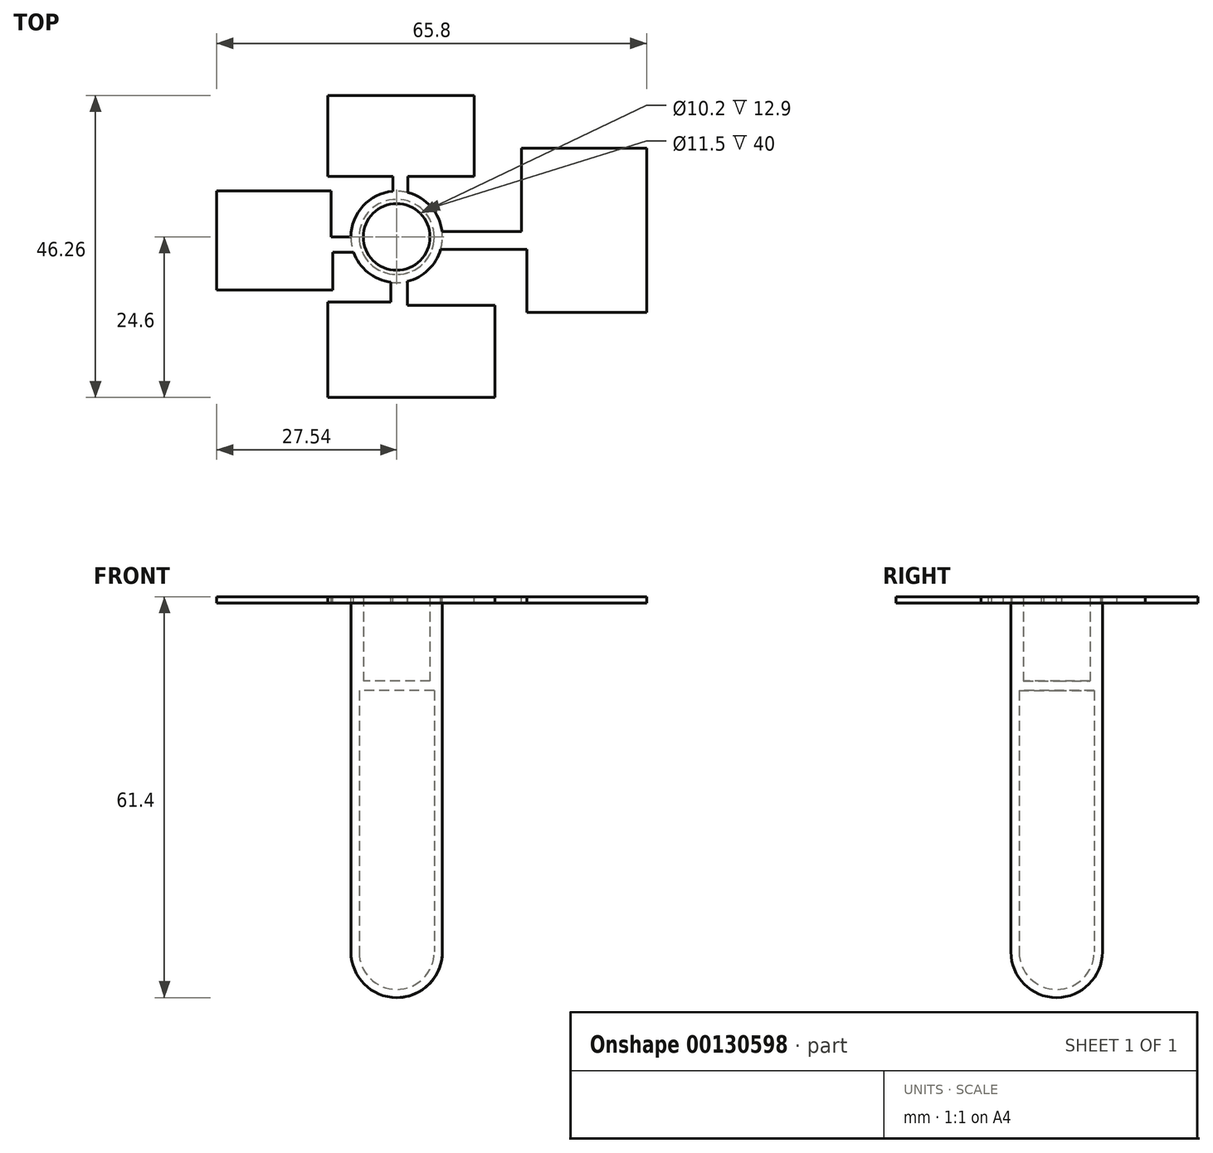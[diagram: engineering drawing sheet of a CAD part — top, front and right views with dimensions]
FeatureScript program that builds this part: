
annotation { "Feature Type Name" : "Feature", "Feature Type Description" : "" }
export const myFeature = defineFeature(function(context is Context, id is Id, definition is map)
    precondition{}
    {
        {
            var Q0;
            Q0=qCreatedBy(makeId("Top.planeOp"),FACE);
            var sketch = newSketch(context, id + "F0", { "sketchPlane" : qUnion([Q0])});
            skCircle(sketch, "E0", {"center": v(0, 0) * mm, "radius": 7 * mm});
            skCircle(sketch, "E1", {"center": v(0, 0) * mm, "radius": 5.75 * mm});
            skLineSegment(sketch, "E2", {"start": v(-5.75, 0) * mm, "end": v(5.75, 0) * mm});
            skSolve(sketch);
        }
        {
            var Q0;
            Q0=makeQuery(id+"F0.imprint","IMPRINT",FACE,{"disambiguationData":[TD([[makeQuery(id+"F0.imprint","IMPRINT",EDGE,{"derivedFrom":sQuery(id+"F0.wireOp",EDGE,"E0")}),1.0]])]});
            var Q1;
            {var subQ0=sQuery(id+"F0.wireOp",EDGE,"E2");Q1=makeQuery(id+"F0.imprint","IMPRINT",FACE,{"disambiguationData":[TD([[makeQuery(id+"F0.imprint","IMPRINT",EDGE,{"derivedFrom":subQ0}),1.0]])]});}
            var Q2;
            {var subQ0=sQuery(id+"F0.wireOp",EDGE,"E2");Q2=makeQuery(id+"F0.imprint","IMPRINT",FACE,{"disambiguationData":[TD([[makeQuery(id+"F0.imprint","IMPRINT",EDGE,{"derivedFrom":subQ0}),-1.0]])]});}
            extrude(context, id + "F1", {"entities" : qUnion([Q0, Q1, Q2]), "oppositeDirection" : true, "depth" : 7 * mm});
        }
        {
            var Q0;
            Q0=makeQuery(id+"F1.opExtrude","CAP_EDGE",EDGE,{"disambiguationData":[OSD([sQuery(id+"F0.wireOp",EDGE,"E0")])],"isStart":false});
            fillet(context, id + "F2", {"entities" : qUnion([Q0]), "radius" : 7 * mm, "tangentPropagation" : true, "allowEdgeOverflow" : false});
        }
        {
            var Q0;
            {var subQ0=sQuery(id+"F0.wireOp",EDGE,"E2");Q0=makeQuery(id+"F0.imprint","IMPRINT",FACE,{"disambiguationData":[TD([[makeQuery(id+"F0.imprint","IMPRINT",EDGE,{"derivedFrom":subQ0}),-1.0]])]});}
            var Q1;
            Q1=sQuery(id+"F0.wireOp",EDGE,"E2");
            revolve(context, id + "F3", {"operationType" : NewBodyOperationType.REMOVE, "entities" : qUnion([Q0]), "axis" : qUnion([Q1]), "revolveType" : RevolveType.FULL, "oppositeDirection" : true});
        }
        {
            var Q0;
            Q0=makeQuery(id+"F1.opExtrude","CAP_FACE",FACE,{"disambiguationData":[OSD([sQuery(id+"F0.wireOp",EDGE,"E0")])],"isStart":true});
            extrude(context, id + "F4", {"entities" : qUnion([Q0]), "operationType" : NewBodyOperationType.ADD, "depth" : 40 * mm, "offsetDistance" : 25 * mm});
        }
        {
            var Q0;
            Q0=makeQuery(id+"F4.opExtrude","CAP_FACE",FACE,{"disambiguationData":[OSD([sQuery(id+"F0.wireOp",EDGE,"E0")])],"isStart":false});
            var sketch = newSketch(context, id + "F5", { "sketchPlane" : qUnion([Q0])});
            skCircle(sketch, "E3", {"center": v(0, 0) * mm, "radius": 5.75 * mm});
            skSolve(sketch);
        }
        {
            var Q0;
            Q0=makeQuery(id+"F5.imprint","IMPRINT",FACE,{"disambiguationData":[TD([[makeQuery(id+"F5.imprint","IMPRINT",EDGE,{"derivedFrom":sQuery(id+"F5.wireOp",EDGE,"E3")}),1.0]])]});
            var Q1;
            Q1=makeQuery(id+"F5.imprint","IMPRINT",FACE,{"disambiguationData":[TD([[makeQuery(id+"F5.imprint","IMPRINT",EDGE,{"derivedFrom":sQuery(id+"F5.wireOp",EDGE,"E3")}),-1.0]])]});
            extrude(context, id + "F6", {"entities" : qUnion([Q0, Q1]), "operationType" : NewBodyOperationType.ADD, "depth" : 1.5 * mm});
        }
        {
            var Q0;
            Q0=makeQuery(id+"F6.opExtrude","CAP_FACE",FACE,{"disambiguationData":[OSD([sQuery(id+"F0.wireOp",EDGE,"E0")])],"isStart":false});
            var sketch = newSketch(context, id + "F7", { "sketchPlane" : qUnion([Q0])});
            skCircle(sketch, "E4", {"center": v(0, 0) * mm, "radius": 5.1 * mm});
            skSolve(sketch);
        }
        {
            var Q0;
            Q0=makeQuery(id+"F7.imprint","IMPRINT",FACE,{"disambiguationData":[TD([[makeQuery(id+"F7.imprint","IMPRINT",EDGE,{"derivedFrom":sQuery(id+"F7.wireOp",EDGE,"E4")}),-1.0]])]});
            extrude(context, id + "F8", {"entities" : qUnion([Q0]), "operationType" : NewBodyOperationType.ADD, "depth" : 12.9 * mm});
        }
        {
            var Q0;
            Q0=makeQuery(id+"F8.opExtrude","CAP_FACE",FACE,{"disambiguationData":[OSD([sQuery(id+"F0.wireOp",EDGE,"E0"),sQuery(id+"F7.wireOp",EDGE,"E4")])],"isStart":false});
            var sketch = newSketch(context, id + "F9", { "sketchPlane" : qUnion([Q0])});
            skLineSegment(sketch, "E5", {"start": v(-0.57, 6.98) * mm, "end": v(-0.57, 9.25) * mm});
            skLineSegment(sketch, "E6", {"start": v(-0.57, 9.25) * mm, "end": v(-7.02, 9.25) * mm});
            skLineSegment(sketch, "E7", {"start": v(-7.02, 9.25) * mm, "end": v(-10.55, 9.25) * mm});
            skLineSegment(sketch, "E8", {"start": v(-10.55, 9.25) * mm, "end": v(-10.55, 21.66) * mm});
            skLineSegment(sketch, "E9", {"start": v(-10.55, 21.66) * mm, "end": v(11.88, 21.66) * mm});
            skLineSegment(sketch, "E10", {"start": v(11.88, 21.66) * mm, "end": v(11.88, 9.25) * mm});
            skLineSegment(sketch, "E11", {"start": v(11.88, 9.25) * mm, "end": v(1.7, 9.25) * mm});
            skLineSegment(sketch, "E12", {"start": v(1.7, 9.25) * mm, "end": v(1.7, 6.79) * mm});
            skLineSegment(sketch, "E13", {"start": v(-7, 0) * mm, "end": v(-10.04, 0) * mm});
            skLineSegment(sketch, "E14", {"start": v(-10.04, 0) * mm, "end": v(-10.04, 7.04) * mm});
            skLineSegment(sketch, "E15", {"start": v(-10.04, 7.04) * mm, "end": v(-27.54, 7.04) * mm});
            skLineSegment(sketch, "E16", {"start": v(-27.54, 7.04) * mm, "end": v(-27.54, -6.56) * mm});
            skLineSegment(sketch, "E17", {"start": v(-27.54, -6.56) * mm, "end": v(-27.54, -8.13) * mm});
            skLineSegment(sketch, "E18", {"start": v(-27.54, -8.13) * mm, "end": v(-9.79, -8.13) * mm});
            skLineSegment(sketch, "E19", {"start": v(-9.79, -8.13) * mm, "end": v(-9.79, -2.32) * mm});
            skLineSegment(sketch, "E20", {"start": v(-9.79, -2.32) * mm, "end": v(-6.6, -2.32) * mm});
            skLineSegment(sketch, "E21", {"start": v(-0.88, -6.94) * mm, "end": v(-0.88, -9.95) * mm});
            skLineSegment(sketch, "E22", {"start": v(-0.88, -9.95) * mm, "end": v(-10.53, -9.95) * mm});
            skLineSegment(sketch, "E23", {"start": v(-10.53, -9.95) * mm, "end": v(-10.53, -24.6) * mm});
            skLineSegment(sketch, "E24", {"start": v(-10.53, -24.6) * mm, "end": v(15.06, -24.6) * mm});
            skLineSegment(sketch, "E25", {"start": v(15.06, -24.6) * mm, "end": v(15.06, -10.45) * mm});
            skLineSegment(sketch, "E26", {"start": v(15.06, -10.45) * mm, "end": v(1.63, -10.45) * mm});
            skLineSegment(sketch, "E27", {"start": v(1.63, -10.45) * mm, "end": v(1.63, -6.8) * mm});
            skLineSegment(sketch, "E28", {"start": v(6.95, 0.8) * mm, "end": v(14.66, 0.8) * mm});
            skLineSegment(sketch, "E29", {"start": v(14.66, 0.8) * mm, "end": v(19.11, 0.8) * mm});
            skLineSegment(sketch, "E30", {"start": v(19.11, 0.8) * mm, "end": v(19.11, 13.56) * mm});
            skLineSegment(sketch, "E31", {"start": v(19.11, 13.56) * mm, "end": v(38.26, 13.56) * mm});
            skLineSegment(sketch, "E32", {"start": v(38.26, 13.56) * mm, "end": v(38.26, -11.59) * mm});
            skLineSegment(sketch, "E33", {"start": v(38.26, -11.59) * mm, "end": v(19.95, -11.59) * mm});
            skLineSegment(sketch, "E34", {"start": v(19.95, -11.59) * mm, "end": v(19.95, -1.9) * mm});
            skLineSegment(sketch, "E35", {"start": v(19.95, -1.9) * mm, "end": v(6.74, -1.9) * mm});
            skSolve(sketch);
        }
        {
            var Q0;
            {var subQ0=sQuery(id+"F9.wireOp",EDGE,"E13");Q0=makeQuery(id+"F9.imprint","IMPRINT",FACE,{"disambiguationData":[TD([[makeQuery(id+"F9.imprint","IMPRINT",EDGE,{"derivedFrom":subQ0}),1.0]])]});}
            var Q1;
            {var subQ0=sQuery(id+"F9.wireOp",EDGE,"E5");Q1=makeQuery(id+"F9.imprint","IMPRINT",FACE,{"disambiguationData":[TD([[makeQuery(id+"F9.imprint","IMPRINT",EDGE,{"derivedFrom":subQ0}),-1.0]])]});}
            var Q2;
            {var subQ0=sQuery(id+"F9.wireOp",EDGE,"E28");Q2=makeQuery(id+"F9.imprint","IMPRINT",FACE,{"disambiguationData":[TD([[makeQuery(id+"F9.imprint","IMPRINT",EDGE,{"derivedFrom":subQ0}),-1.0]])]});}
            var Q3;
            {var subQ0=sQuery(id+"F9.wireOp",EDGE,"E21");Q3=makeQuery(id+"F9.imprint","IMPRINT",FACE,{"disambiguationData":[TD([[makeQuery(id+"F9.imprint","IMPRINT",EDGE,{"derivedFrom":subQ0}),1.0]])]});}
            extrude(context, id + "F10", {"entities" : qUnion([Q0, Q1, Q2, Q3]), "operationType" : NewBodyOperationType.ADD, "oppositeDirection" : true, "depth" : 1 * mm});
        }
    });
